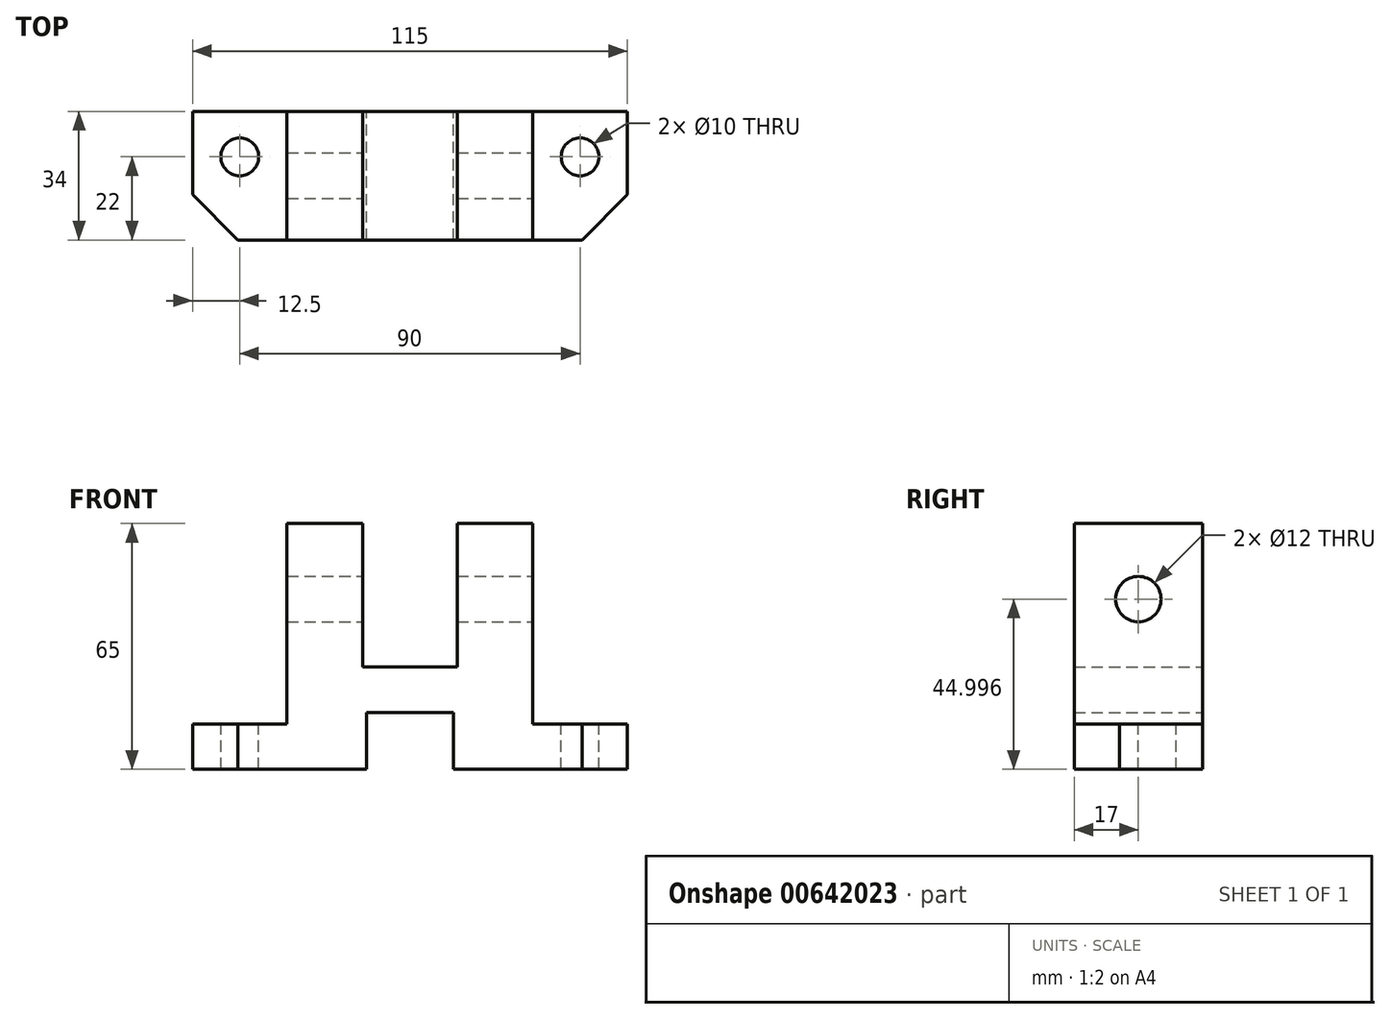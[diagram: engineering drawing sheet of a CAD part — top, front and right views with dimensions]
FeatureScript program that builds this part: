
annotation { "Feature Type Name" : "Feature", "Feature Type Description" : "" }
export const myFeature = defineFeature(function(context is Context, id is Id, definition is map)
    precondition{}
    {
        {
            var Q0;
            Q0=qCreatedBy(makeId("Front.planeOp"),FACE);
            var sketch = newSketch(context, id + "F0", { "sketchPlane" : qUnion([Q0])});
            skLineSegment(sketch, "E0", {"start": v(0, 32.38) * mm, "end": v(0, -83.37) * mm, "construction": true});
            skLineSegment(sketch, "E1", {"start": v(-32.5, -2.22) * mm, "end": v(-32.5, -55.22) * mm});
            skLineSegment(sketch, "E2", {"start": v(-32.5, -55.22) * mm, "end": v(-57.5, -55.22) * mm});
            skLineSegment(sketch, "E3", {"start": v(-57.5, -55.22) * mm, "end": v(-57.5, -67.22) * mm});
            skLineSegment(sketch, "E4", {"start": v(-57.5, -67.22) * mm, "end": v(-11.52, -67.22) * mm});
            skLineSegment(sketch, "E5", {"start": v(-11.52, -67.22) * mm, "end": v(-11.52, -52.22) * mm});
            skLineSegment(sketch, "E6", {"start": v(-11.52, -52.22) * mm, "end": v(0, -52.22) * mm});
            skLineSegment(sketch, "E7.MirrorCS", {"start": v(32.5, -2.22) * mm, "end": v(32.5, -55.22) * mm});
            skLineSegment(sketch, "E8.MirrorCS", {"start": v(32.5, -55.22) * mm, "end": v(57.5, -55.22) * mm});
            skLineSegment(sketch, "E9.MirrorCS", {"start": v(57.5, -55.22) * mm, "end": v(57.5, -67.22) * mm});
            skLineSegment(sketch, "E10.MirrorCS", {"start": v(57.5, -67.22) * mm, "end": v(11.52, -67.22) * mm});
            skLineSegment(sketch, "E11.MirrorCS", {"start": v(11.52, -67.22) * mm, "end": v(11.52, -52.22) * mm});
            skLineSegment(sketch, "E12.MirrorCS", {"start": v(11.52, -52.22) * mm, "end": v(0, -52.22) * mm});
            skLineSegment(sketch, "E13", {"start": v(-32.5, -2.22) * mm, "end": v(-12.5, -2.22) * mm});
            skLineSegment(sketch, "E14", {"start": v(-12.5, -2.22) * mm, "end": v(-12.5, -40.22) * mm});
            skLineSegment(sketch, "E15", {"start": v(-12.5, -40.22) * mm, "end": v(0, -40.22) * mm});
            skLineSegment(sketch, "E16.MirrorCS", {"start": v(12.5, -40.22) * mm, "end": v(0, -40.22) * mm});
            skLineSegment(sketch, "E17.MirrorCS", {"start": v(12.5, -2.22) * mm, "end": v(12.5, -40.22) * mm});
            skLineSegment(sketch, "E18.MirrorCS", {"start": v(32.5, -2.22) * mm, "end": v(12.5, -2.22) * mm});
            skSolve(sketch);
        }
        {
            var Q0;
            Q0 = qSketchRegion(id + "F0", true);
            extrude(context, id + "F1", {"entities" : qUnion([Q0]), "depth" : 34 * mm, "offsetDistance" : 25 * mm});
        }
        {
            var Q0;
            Q0=makeQuery(id+"F1.opExtrude","SWEPT_FACE",FACE,{"disambiguationData":[OSD([sQuery(id+"F0.wireOp",EDGE,"E7.MirrorCS")])]});
            var sketch = newSketch(context, id + "F2", { "sketchPlane" : qUnion([Q0])});
            skPoint(sketch, "E19.startSnap0", {"position": v(-17, -2.22) * mm});
            skLineSegment(sketch, "E20", {"start": v(-17, 13.79) * mm, "end": v(-17, -22.22) * mm, "construction": true});
            skCircle(sketch, "E21", {"center": v(-17, -22.22) * mm, "radius": 6 * mm});
            skSolve(sketch);
        }
        {
            var Q0;
            Q0=makeQuery(id+"F2.imprint","IMPRINT",FACE,{"disambiguationData":[TD([[makeQuery(id+"F2.imprint","IMPRINT",EDGE,{"derivedFrom":sQuery(id+"F2.wireOp",EDGE,"E21")}),1.0]])]});
            extrude(context, id + "F3", {"entities" : qUnion([Q0]), "operationType" : NewBodyOperationType.REMOVE, "endBound" : BoundingType.THROUGH_ALL, "oppositeDirection" : true, "depth" : 25 * mm, "offsetDistance" : 25 * mm});
        }
        {
            var Q0;
            Q0=qCreatedBy(makeId("Top.planeOp"),FACE);
            var sketch = newSketch(context, id + "F4", { "sketchPlane" : qUnion([Q0])});
            skPoint(sketch, "E22.startSnap0", {"position": v(32.5, -17) * mm});
            skLineSegment(sketch, "E23", {"start": v(0, 12.67) * mm, "end": v(0, -45.2) * mm, "construction": true});
            skCircle(sketch, "E24", {"center": v(-45, -12) * mm, "radius": 5 * mm});
            skCircle(sketch, "E25.MirrorC", {"center": v(45, -12) * mm, "radius": 5 * mm});
            skSolve(sketch);
        }
        {
            var Q0;
            Q0 = qSketchRegion(id + "F4", true);
            extrude(context, id + "F5", {"entities" : qUnion([Q0]), "operationType" : NewBodyOperationType.REMOVE, "endBound" : BoundingType.THROUGH_ALL, "oppositeDirection" : true, "depth" : 25 * mm, "offsetDistance" : 25 * mm});
        }
        {
            var Q0;
            Q0=qCreatedBy(makeId("Top.planeOp"),FACE);
            var sketch = newSketch(context, id + "F6", { "sketchPlane" : qUnion([Q0])});
            skLineSegment(sketch, "E26", {"start": v(0, 28.77) * mm, "end": v(0, -49.18) * mm, "construction": true});
            skLineSegment(sketch, "E27", {"start": v(57.5, -22) * mm, "end": v(45.5, -34) * mm});
            skLineSegment(sketch, "E28.MirrorCS", {"start": v(-57.5, -22) * mm, "end": v(-45.5, -34) * mm});
            skLineSegment(sketch, "E29", {"start": v(-57.5, -22) * mm, "end": v(-57.5, -34) * mm});
            skLineSegment(sketch, "E30", {"start": v(-57.5, -34) * mm, "end": v(-45.5, -34) * mm});
            skLineSegment(sketch, "E31.MirrorCS", {"start": v(57.5, -34) * mm, "end": v(45.5, -34) * mm});
            skLineSegment(sketch, "E32.MirrorCS", {"start": v(57.5, -22) * mm, "end": v(57.5, -34) * mm});
            skSolve(sketch);
        }
        {
            var Q0;
            Q0 = qSketchRegion(id + "F6", true);
            extrude(context, id + "F7", {"entities" : qUnion([Q0]), "operationType" : NewBodyOperationType.REMOVE, "endBound" : BoundingType.THROUGH_ALL, "oppositeDirection" : true, "depth" : 25 * mm, "offsetDistance" : 25 * mm});
        }
    });
